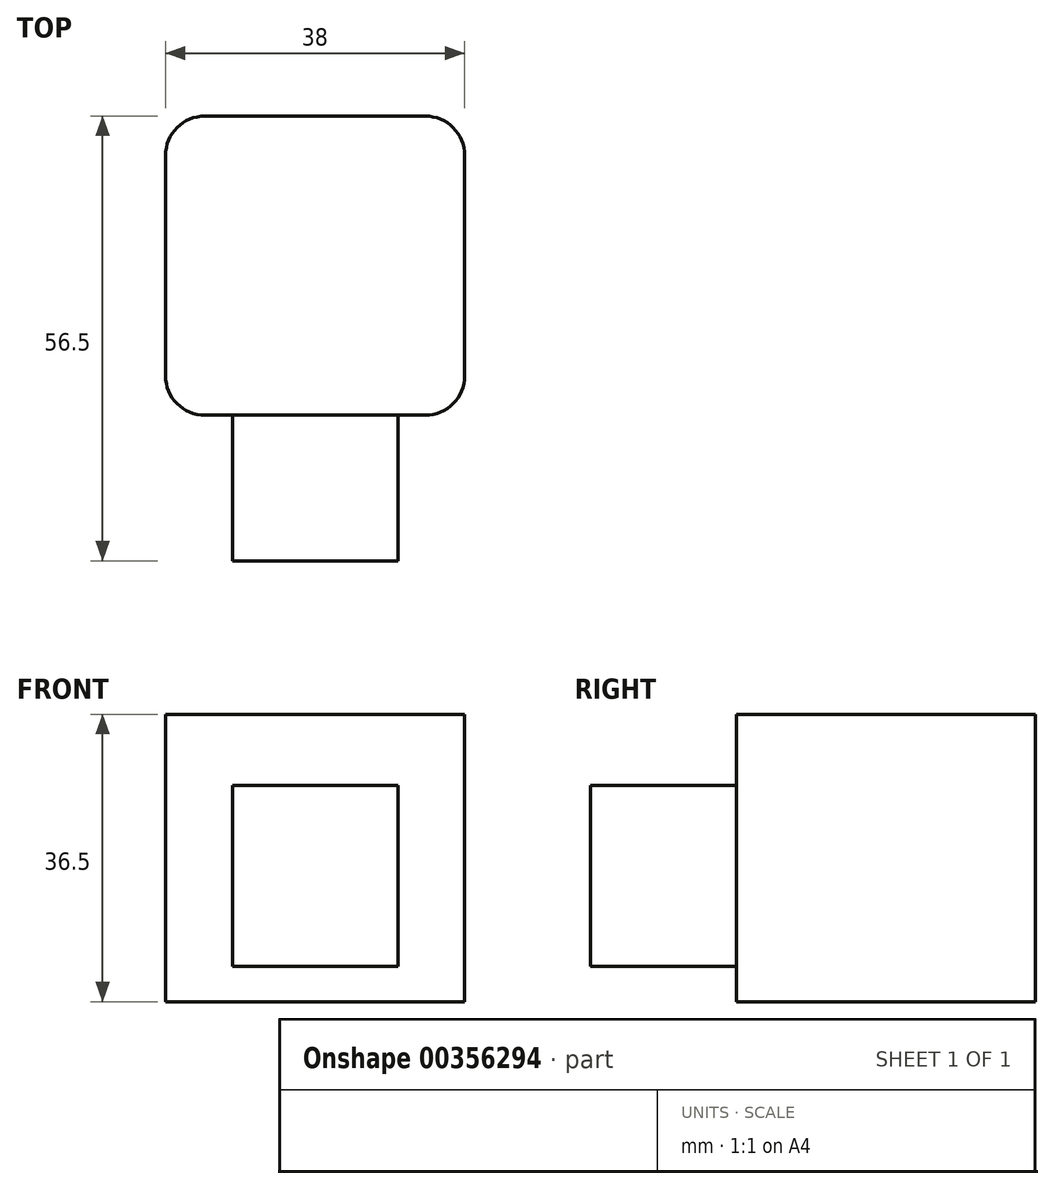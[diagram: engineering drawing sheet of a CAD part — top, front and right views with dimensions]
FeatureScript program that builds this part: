
annotation { "Feature Type Name" : "Feature", "Feature Type Description" : "" }
export const myFeature = defineFeature(function(context is Context, id is Id, definition is map)
    precondition{}
    {
        {
            var Q0;
            Q0=qCreatedBy(makeId("Top.planeOp"),FACE);
            var sketch = newSketch(context, id + "F0", { "sketchPlane" : qUnion([Q0])});
            skLineSegment(sketch, "E0.bottom", {"start": v(19, -19) * mm, "end": v(-19, -19) * mm});
            skLineSegment(sketch, "E0.top", {"start": v(19, 19) * mm, "end": v(-19, 19) * mm});
            skLineSegment(sketch, "E0.left", {"start": v(19, -19) * mm, "end": v(19, 19) * mm});
            skLineSegment(sketch, "E0.right", {"start": v(-19, -19) * mm, "end": v(-19, 19) * mm});
            skPoint(sketch, "E0.middle", {"position": v(0, 0) * mm});
            skSolve(sketch);
        }
        {
            var Q0;
            Q0 = qSketchRegion(id + "F0", true);
            extrude(context, id + "F1", {"entities" : qUnion([Q0]), "depth" : 36.5 * mm});
        }
        {
            var Q0;
            Q0=makeQuery(id+"F1.opExtrude","SWEPT_EDGE",EDGE,{"disambiguationData":[OSD([sQuery(id+"F0.wireOp",EDGE,"E0.bottom"),sQuery(id+"F0.wireOp",EDGE,"E0.left")])]});
            var Q1;
            Q1=makeQuery(id+"F1.opExtrude","SWEPT_EDGE",EDGE,{"disambiguationData":[OSD([sQuery(id+"F0.wireOp",EDGE,"E0.top"),sQuery(id+"F0.wireOp",EDGE,"E0.left")])]});
            var Q2;
            Q2=makeQuery(id+"F1.opExtrude","SWEPT_EDGE",EDGE,{"disambiguationData":[OSD([sQuery(id+"F0.wireOp",EDGE,"E0.top"),sQuery(id+"F0.wireOp",EDGE,"E0.right")])]});
            var Q3;
            Q3=makeQuery(id+"F1.opExtrude","SWEPT_EDGE",EDGE,{"disambiguationData":[OSD([sQuery(id+"F0.wireOp",EDGE,"E0.bottom"),sQuery(id+"F0.wireOp",EDGE,"E0.right")])]});
            fillet(context, id + "F2", {"entities" : qUnion([Q0, Q1, Q2, Q3]), "radius" : 5 * mm, "tangentPropagation" : true, "allowEdgeOverflow" : false});
        }
        {
            var Q0;
            Q0=makeQuery(id+"F1.opExtrude","SWEPT_FACE",FACE,{"disambiguationData":[OSD([sQuery(id+"F0.wireOp",EDGE,"E0.bottom")])]});
            var sketch = newSketch(context, id + "F3", { "sketchPlane" : qUnion([Q0])});
            skLineSegment(sketch, "E1.bottom", {"start": v(-10.5, 27.5) * mm, "end": v(10.5, 27.5) * mm});
            skLineSegment(sketch, "E1.top", {"start": v(-10.5, 4.5) * mm, "end": v(10.5, 4.5) * mm});
            skLineSegment(sketch, "E1.left", {"start": v(-10.5, 27.5) * mm, "end": v(-10.5, 4.5) * mm});
            skLineSegment(sketch, "E1.right", {"start": v(10.5, 27.5) * mm, "end": v(10.5, 4.5) * mm});
            skPoint(sketch, "E1.middle", {"position": v(0, 16) * mm});
            skSolve(sketch);
        }
        {
            var Q0;
            Q0 = qSketchRegion(id + "F3", true);
            extrude(context, id + "F4", {"entities" : qUnion([Q0]), "operationType" : NewBodyOperationType.ADD, "depth" : 18.5 * mm});
        }
    });
